# Revit family: 61172XXX_
name_source: partatom
category: Plumbing Fixtures
units: mm (PartAtom-declared; Revit-internal decimal feet)

## family parameters
Always vertical = No
Cut with Voids When Loaded = No
OmniClass Number = 23.31.23.00
OmniClass Title = Bidets
Part Type = Normal
Room Calculation Point = No
Round Connector Dimension = Use Diameter
Shared = No
Work Plane-Based = Yes

## types (1)
- 450 White
    Connector Description = Water Outlet 46 mm
    Default Elevation = 1219 mm
    Description = EluPura Original Q Wall hung Bidet 540 with tap hole and overflow, SmartClean
    Diameter = 46 mm  [stored 0.150919 ft]
    Manufacturer = Hansgrohe
    Material = Hansgrohe - Ceramic - 450 White
    Model = 61172XXX
    Product Guid = 2173b364-fc8c-428b-9e89-551053892845
    Product Page URL = https://www.hansgrohe.com
    Product data url = https://bimobject.com
    URL = https://www.hansgrohe.com
    Version = 1

note: [stored X ft] marks values corroborated as IEEE doubles in the binary element streams (Revit-internal decimal feet)

## geometry (parser evidence)
native form markers: Sweep x2
no freeform markers — native parametric forms only
